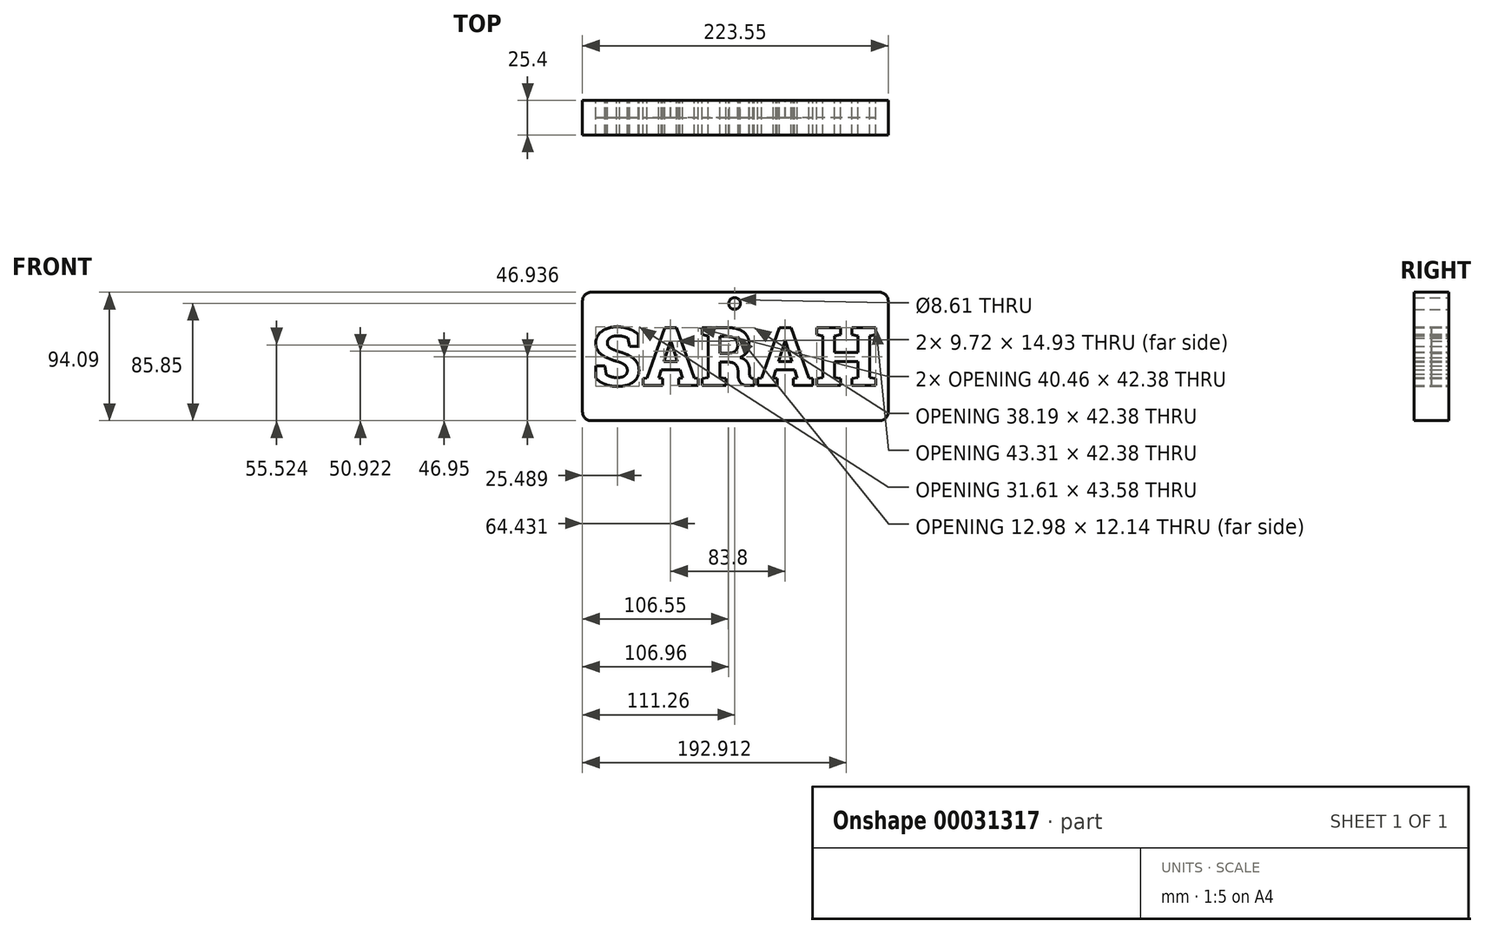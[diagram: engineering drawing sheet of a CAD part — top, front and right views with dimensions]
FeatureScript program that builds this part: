
annotation { "Feature Type Name" : "Feature", "Feature Type Description" : "" }
export const myFeature = defineFeature(function(context is Context, id is Id, definition is map)
    precondition{}
    {
        {
            var Q0;
            Q0=qCreatedBy(makeId("Front.planeOp"),FACE);
            var sketch = newSketch(context, id + "F0", { "sketchPlane" : qUnion([Q0])});
            skText(sketch, "E0", { "text": "SARAH", "fontName": "RobotoSlab-Bold.ttf"});
            skLineSegment(sketch, "E1.bottom", {"start": v(-104.9, 71.08) * mm, "end": v(105.94, 71.08) * mm});
            skLineSegment(sketch, "E1.top", {"start": v(-104.9, -23) * mm, "end": v(105.94, -23) * mm});
            skLineSegment(sketch, "E1.left", {"start": v(-111.26, 64.73) * mm, "end": v(-111.26, -16.66) * mm});
            skLineSegment(sketch, "E1.right", {"start": v(112.29, 64.73) * mm, "end": v(112.29, -16.66) * mm});
            skCircle(sketch, "E2", {"center": v(0, 62.84) * mm, "radius": 4.3 * mm});
            skPoint(sketch, "E3.visualSharp", {"position": v(-111.26, 71.08) * mm});
            skArc(sketch, "E3.filletArc", {"start": v(-104.9, 71.08) * mm, "mid": v(-109.4, 69.22) * mm, "end": v(-111.26, 64.73) * mm});
            skPoint(sketch, "E4.visualSharp", {"position": v(-111.26, -23) * mm});
            skArc(sketch, "E4.filletArc", {"start": v(-111.26, -16.66) * mm, "mid": v(-109.4, -21.15) * mm, "end": v(-104.9, -23) * mm});
            skPoint(sketch, "E5.visualSharp", {"position": v(112.29, -23) * mm});
            skArc(sketch, "E5.filletArc", {"start": v(105.94, -23) * mm, "mid": v(110.43, -21.15) * mm, "end": v(112.29, -16.66) * mm});
            skPoint(sketch, "E6.visualSharp", {"position": v(112.29, 71.08) * mm});
            skArc(sketch, "E6.filletArc", {"start": v(112.29, 64.73) * mm, "mid": v(110.43, 69.22) * mm, "end": v(105.94, 71.08) * mm});
            const initialGuessF0  = {"E0": [-0.1044, 0.00275, 1, 0, 0.04292]};
            skSetInitialGuess(sketch, initialGuessF0);
            skSolve(sketch);
        }
        {
            var Q0;
            Q0=makeQuery(id+"F0.imprint","IMPRINT",FACE,{"disambiguationData":[TD([[makeQuery(id+"F0.imprint","IMPRINT",EDGE,{"derivedFrom":sQuery(id+"F0.wireOp",EDGE,"E0.sketch_text.stroke-0")}),-1.0]])]});
            var Q1;
            Q1=makeQuery(id+"F0.imprint","IMPRINT",FACE,{"disambiguationData":[TD([[makeQuery(id+"F0.imprint","IMPRINT",EDGE,{"derivedFrom":sQuery(id+"F0.wireOp",EDGE,"E0.sketch_text.stroke-30")}),-1.0]])]});
            var Q2;
            Q2=makeQuery(id+"F0.imprint","IMPRINT",FACE,{"disambiguationData":[TD([[makeQuery(id+"F0.imprint","IMPRINT",EDGE,{"derivedFrom":sQuery(id+"F0.wireOp",EDGE,"E0.sketch_text.stroke-50")}),-1.0]])]});
            var Q3;
            Q3=makeQuery(id+"F0.imprint","IMPRINT",FACE,{"disambiguationData":[TD([[makeQuery(id+"F0.imprint","IMPRINT",EDGE,{"derivedFrom":sQuery(id+"F0.wireOp",EDGE,"E0.sketch_text.stroke-86")}),-1.0]])]});
            var Q4;
            Q4=makeQuery(id+"F0.imprint","IMPRINT",FACE,{"disambiguationData":[TD([[makeQuery(id+"F0.imprint","IMPRINT",EDGE,{"derivedFrom":sQuery(id+"F0.wireOp",EDGE,"E0.sketch_text.stroke-106")}),-1.0]])]});
            extrude(context, id + "F1", {"entities" : qUnion([Q0, Q1, Q2, Q3, Q4]), "depth" : 12.7 * mm});
        }
        {
            var Q0;
            Q0 = qSketchRegion(id + "F0", true);
            extrude(context, id + "F2", {"entities" : qUnion([Q0]), "depth" : 25.4 * mm});
        }
    });
